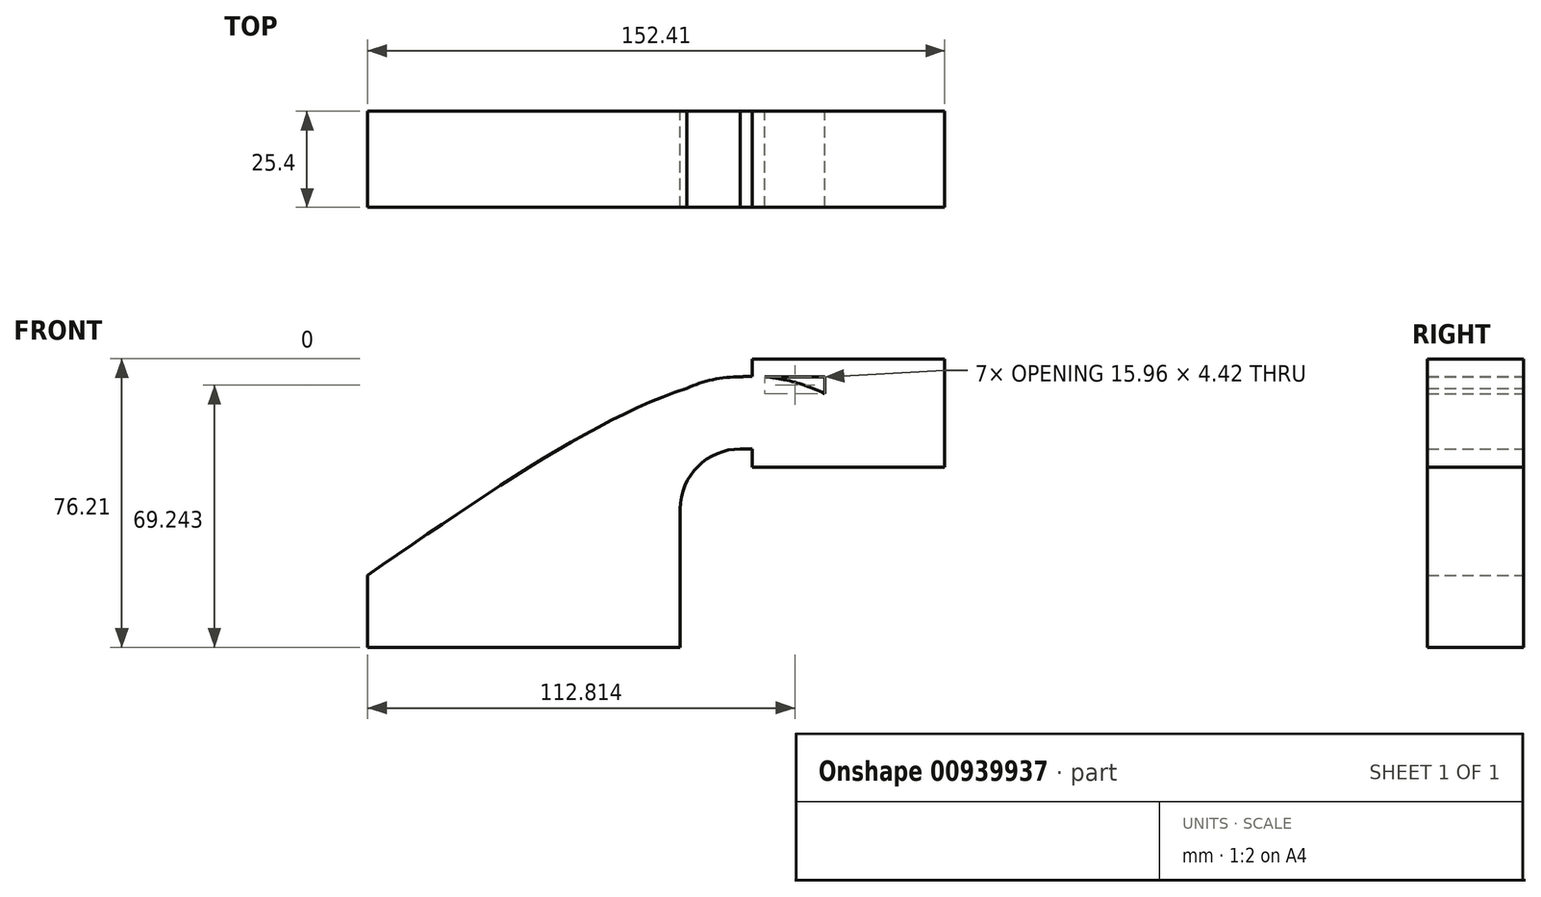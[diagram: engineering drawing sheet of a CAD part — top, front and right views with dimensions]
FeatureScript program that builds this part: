
annotation { "Feature Type Name" : "Feature", "Feature Type Description" : "" }
export const myFeature = defineFeature(function(context is Context, id is Id, definition is map)
    precondition{}
    {
        {
            var Q0;
            Q0=qCreatedBy(makeId("Front.planeOp"),FACE);
            var sketch = newSketch(context, id + "F0", { "sketchPlane" : qUnion([Q0])});
            skLineSegment(sketch, "E0.bottom", {"start": v(-41.28, 9.52) * mm, "end": v(41.28, 9.53) * mm});
            skLineSegment(sketch, "E0.top", {"start": v(-41.28, -9.53) * mm, "end": v(41.28, -9.53) * mm});
            skLineSegment(sketch, "E0.left", {"start": v(-41.28, 9.52) * mm, "end": v(-41.28, -9.53) * mm});
            skLineSegment(sketch, "E0.right", {"start": v(41.28, 9.53) * mm, "end": v(41.28, -9.52) * mm});
            skPoint(sketch, "E0.middle", {"position": v(0, 0) * mm});
            skLineSegment(sketch, "E1.bottom", {"start": v(60.33, 38.1) * mm, "end": v(111.12, 38.1) * mm});
            skLineSegment(sketch, "E1.top", {"start": v(60.32, 66.67) * mm, "end": v(111.12, 66.67) * mm});
            skLineSegment(sketch, "E1.left", {"start": v(60.33, 38.1) * mm, "end": v(60.32, 66.68) * mm});
            skLineSegment(sketch, "E1.right", {"start": v(111.12, 38.1) * mm, "end": v(111.12, 66.68) * mm});
            skPoint(sketch, "E1.middle", {"position": v(85.72, 52.39) * mm});
            skLineSegment(sketch, "E2", {"start": v(41.27, 9.53) * mm, "end": v(41.27, 27) * mm});
            skArc(sketch, "E3", {"start": v(41.27, 27) * mm, "mid": v(45.92, 38.23) * mm, "end": v(57.15, 42.88) * mm});
            skPoint(sketch, "E4.endSnap0", {"position": v(85.72, 38.1) * mm});
            skLineSegment(sketch, "E5", {"start": v(57.15, 42.88) * mm, "end": v(79.51, 42.88) * mm});
            skLineSegment(sketch, "E6.0", {"start": v(57.15, 61.93) * mm, "end": v(79.51, 61.93) * mm});
            skArc(sketch, "E6.1", {"start": v(22.23, 27) * mm, "mid": v(32.45, 51.7) * mm, "end": v(57.15, 61.93) * mm});
            skLineSegment(sketch, "E6.2", {"start": v(22.23, 9.53) * mm, "end": v(22.23, 27) * mm});
            skLineSegment(sketch, "E7", {"start": v(79.51, 42.88) * mm, "end": v(79.51, 61.93) * mm});
            skFitSpline(sketch, "E8", {"points": [v(-41.28, 9.53) * mm, v(57.15, 61.93) * mm, v(94.28, 48.95) * mm], "startDerivative": vector(174.84, 120.64) * mm, "endDerivative": vector(89, -56.87) * mm});
            skSolve(sketch);
        }
        {
            var Q0;
            Q0 = qSketchRegion(id + "F0", true);
            extrude(context, id + "F1", {"entities" : qUnion([Q0]), "depth" : 25.4 * mm, "offsetDistance" : 25.4 * mm});
        }
    });
